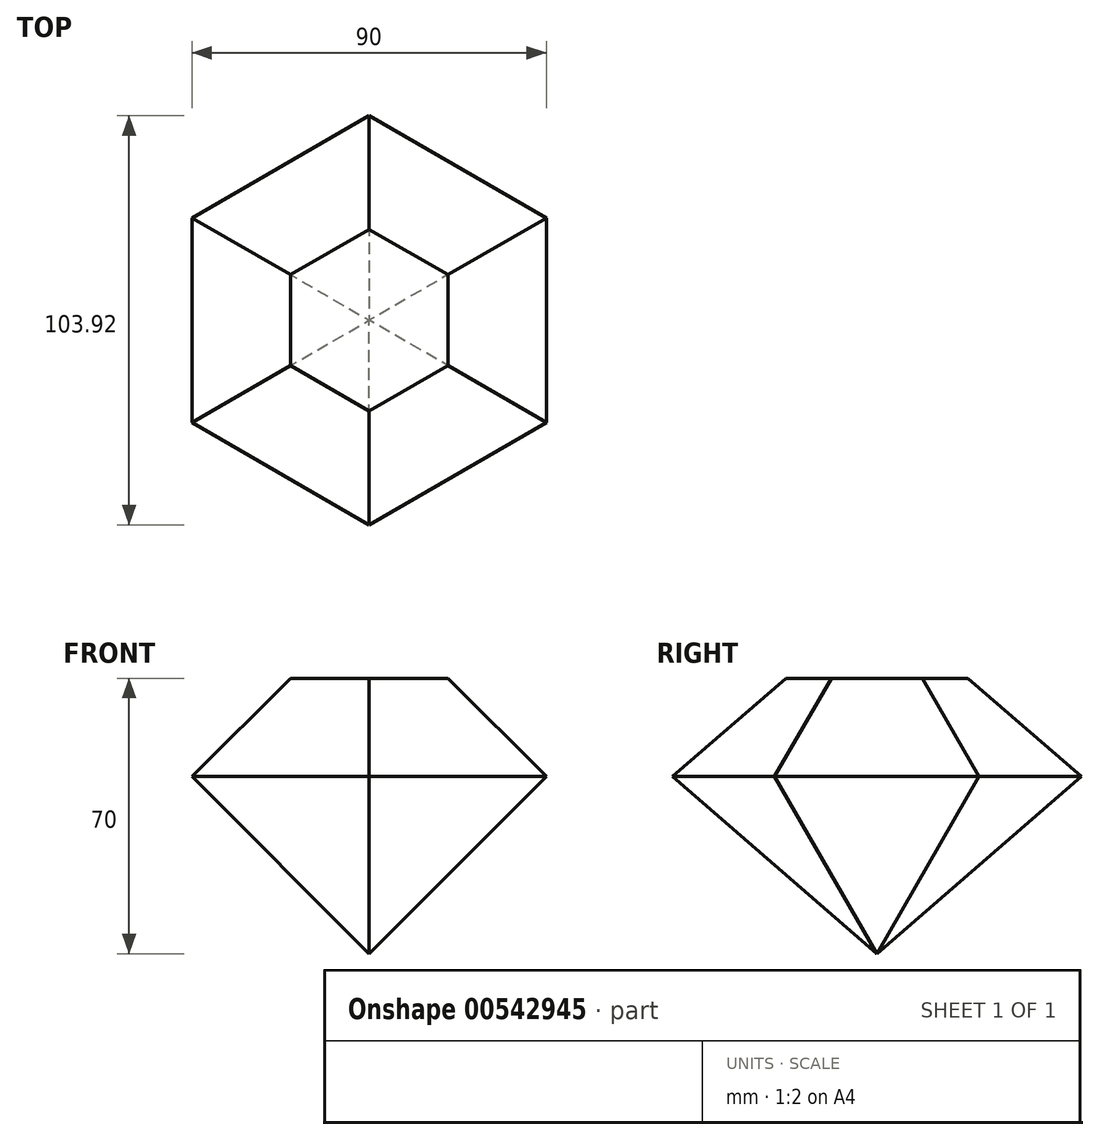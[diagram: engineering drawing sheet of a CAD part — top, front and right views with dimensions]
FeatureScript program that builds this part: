
annotation { "Feature Type Name" : "Feature", "Feature Type Description" : "" }
export const myFeature = defineFeature(function(context is Context, id is Id, definition is map)
    precondition{}
    {
        {
            var Q0;
            Q0=qCreatedBy(makeId("Top.planeOp"),FACE);
            var sketch = newSketch(context, id + "F0", { "sketchPlane" : qUnion([Q0])});
            skLineSegment(sketch, "E0.0", {"start": v(0, 51.96) * mm, "end": v(45, 25.98) * mm});
            skLineSegment(sketch, "E0.1", {"start": v(45, 25.98) * mm, "end": v(45, -25.98) * mm});
            skLineSegment(sketch, "E0.2", {"start": v(45, -25.98) * mm, "end": v(0, -51.96) * mm});
            skLineSegment(sketch, "E0.3", {"start": v(0, -51.96) * mm, "end": v(-45, -25.98) * mm});
            skLineSegment(sketch, "E0.4", {"start": v(-45, -25.98) * mm, "end": v(-45, 25.98) * mm});
            skLineSegment(sketch, "E0.5", {"start": v(-45, 25.98) * mm, "end": v(0, 51.96) * mm});
            skPoint(sketch, "E0.0.midPoint", {"position": v(22.5, 38.97) * mm});
            skPoint(sketch, "E0.cCircle.center.orphan", {"position": v(0, 0) * mm});
            skSolve(sketch);
        }
        {
            var Q0;
            Q0=makeQuery(id+"F0.imprint","IMPRINT",FACE,{"disambiguationData":[TD([[makeQuery(id+"F0.imprint","IMPRINT",EDGE,{"derivedFrom":sQuery(id+"F0.wireOp",EDGE,"E0.0")}),-1.0]])]});
            extrude(context, id + "F1", {"entities" : qUnion([Q0]), "depth" : 25 * mm, "offsetDistance" : 25 * mm, "hasDraft" : true, "draftAngle" : 45 * degree, "draftPullDirection" : true, "hasSecondDirection" : true, "secondDirectionOppositeDirection" : true, "secondDirectionDepth" : 45 * mm, "hasSecondDirectionDraft" : true, "secondDirectionDraftAngle" : 45 * degree, "secondDirectionDraftPullDirection" : true});
        }
    });
